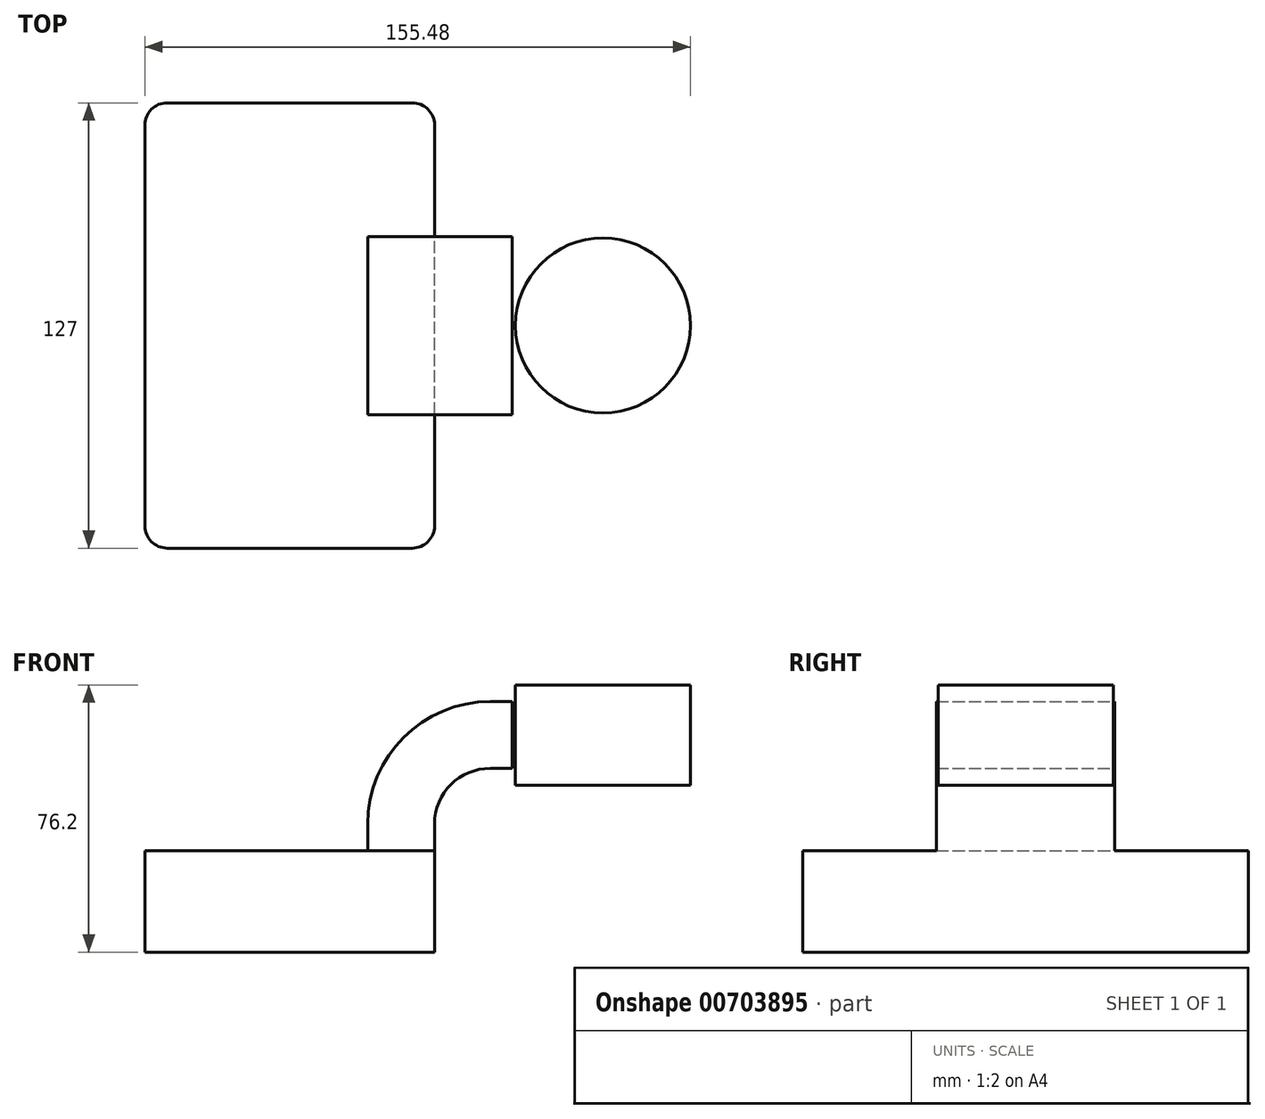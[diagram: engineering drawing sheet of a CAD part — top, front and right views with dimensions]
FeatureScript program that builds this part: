
annotation { "Feature Type Name" : "Feature", "Feature Type Description" : "" }
export const myFeature = defineFeature(function(context is Context, id is Id, definition is map)
    precondition{}
    {
        {
            var Q0;
            Q0=qCreatedBy(makeId("Front.planeOp"),FACE);
            var sketch = newSketch(context, id + "F0", { "sketchPlane" : qUnion([Q0])});
            skLineSegment(sketch, "E0.bottom", {"start": v(-41.27, 14.47) * mm, "end": v(41.27, 14.47) * mm});
            skLineSegment(sketch, "E0.top", {"start": v(-41.27, -14.47) * mm, "end": v(41.27, -14.47) * mm});
            skLineSegment(sketch, "E0.left", {"start": v(-41.28, 14.47) * mm, "end": v(-41.28, -14.47) * mm});
            skLineSegment(sketch, "E0.right", {"start": v(41.28, 14.47) * mm, "end": v(41.28, -14.47) * mm});
            skPoint(sketch, "E0.middle", {"position": v(0, 0) * mm});
            skLineSegment(sketch, "E1.bottom", {"start": v(114.21, 33.16) * mm, "end": v(63.41, 33.16) * mm});
            skLineSegment(sketch, "E1.top", {"start": v(114.21, 61.73) * mm, "end": v(63.41, 61.73) * mm});
            skLineSegment(sketch, "E1.left", {"start": v(114.21, 33.16) * mm, "end": v(114.21, 61.73) * mm});
            skLineSegment(sketch, "E1.right", {"start": v(63.41, 33.16) * mm, "end": v(63.41, 61.73) * mm});
            skPoint(sketch, "E1.middle", {"position": v(88.81, 47.44) * mm});
            skLineSegment(sketch, "E2", {"start": v(41.28, 14.47) * mm, "end": v(41.28, 22.06) * mm});
            skArc(sketch, "E3", {"start": v(41.28, 22.06) * mm, "mid": v(45.92, 33.28) * mm, "end": v(57.15, 37.93) * mm});
            skLineSegment(sketch, "E4", {"start": v(57.15, 37.93) * mm, "end": v(89.27, 37.93) * mm});
            skLineSegment(sketch, "E5", {"start": v(89.27, 37.93) * mm, "end": v(66.96, 37.93) * mm});
            skLineSegment(sketch, "E6.0", {"start": v(57.15, 56.98) * mm, "end": v(89.27, 56.98) * mm});
            skArc(sketch, "E6.1", {"start": v(22.23, 22.06) * mm, "mid": v(32.45, 46.75) * mm, "end": v(57.15, 56.98) * mm});
            skLineSegment(sketch, "E6.2", {"start": v(22.23, 14.47) * mm, "end": v(22.23, 22.06) * mm});
            skLineSegment(sketch, "E7", {"start": v(89.27, 33.16) * mm, "end": v(89.27, 61.73) * mm});
            skFitSpline(sketch, "E8", {"points": [v(-41.27, 14.47) * mm, v(57.15, 56.98) * mm], "startDerivative": vector(69.74, 94.52) * mm, "endDerivative": vector(102.79, -27.74) * mm});
            skSolve(sketch);
        }
        {
            var Q0;
            Q0=makeQuery(id+"F0.imprint","IMPRINT",FACE,{"disambiguationData":[TD([[makeQuery(id+"F0.imprint","IMPRINT",EDGE,{"derivedFrom":sQuery(id+"F0.wireOp",EDGE,"E0.top")}),1.0]])]});
            extrude(context, id + "F1", {"entities" : qUnion([Q0]), "endBound" : BoundingType.SYMMETRIC, "depth" : 127 * mm, "offsetDistance" : 25.4 * mm});
        }
        {
            var Q0;
            {var subQ1=sQuery(id+"F0.wireOp",EDGE,"E2");Q0=makeQuery(id+"F0.imprint","IMPRINT",FACE,{"disambiguationData":[TD([[makeQuery(id+"F0.imprint","IMPRINT",EDGE,{"derivedFrom":subQ1}),1.0]])]});}
            var sketch = newSketch(context, id + "F2", { "sketchPlane" : qUnion([Q0])});
            skSolve(sketch);
        }
        {
            var Q0;
            Q0 = qSketchRegion(id + "F2", true);
            var Q1;
            {var subQ1=sQuery(id+"F0.wireOp",EDGE,"E2");Q1=makeQuery(id+"F0.imprint","IMPRINT",FACE,{"disambiguationData":[TD([[makeQuery(id+"F0.imprint","IMPRINT",EDGE,{"derivedFrom":subQ1}),1.0]])]});}
            var Q2;
            {var subQ5=sQuery(id+"F0.wireOp",EDGE,"E5");Q2=makeQuery(id+"F0.imprint","IMPRINT",FACE,{"disambiguationData":[TD([[makeQuery(id+"F0.imprint","IMPRINT",EDGE,{"derivedFrom":subQ5}),-1.0]])]});}
            extrude(context, id + "F3", {"entities" : qUnion([Q0, Q1, Q2]), "operationType" : NewBodyOperationType.ADD, "endBound" : BoundingType.SYMMETRIC, "depth" : 50.8 * mm, "offsetDistance" : 25.4 * mm});
        }
        {
            var Q0;
            Q0=makeQuery(id+"F0.imprint","IMPRINT",FACE,{"disambiguationData":[TD([[makeQuery(id+"F0.imprint","IMPRINT",EDGE,{"derivedFrom":sQuery(id+"F0.wireOp",EDGE,"E6.1")}),1.0]])]});
            var sketch = newSketch(context, id + "F4", { "sketchPlane" : qUnion([Q0])});
            skSolve(sketch);
        }
        {
            var Q0;
            Q0 = qSketchRegion(id + "F4", true);
            var Q1;
            Q1=makeQuery(id+"F0.imprint","IMPRINT",FACE,{"disambiguationData":[TD([[makeQuery(id+"F0.imprint","IMPRINT",EDGE,{"derivedFrom":sQuery(id+"F0.wireOp",EDGE,"E6.1")}),1.0]])]});
            extrude(context, id + "F5", {"entities" : qUnion([Q0, Q1]), "operationType" : NewBodyOperationType.ADD, "endBound" : BoundingType.SYMMETRIC, "depth" : 15.88 * mm, "offsetDistance" : 25.4 * mm});
        }
        {
            var Q0;
            {var subQ0=sQuery(id+"F0.wireOp",EDGE,"E1.left");Q0=makeQuery(id+"F0.imprint","IMPRINT",FACE,{"disambiguationData":[TD([[makeQuery(id+"F0.imprint","IMPRINT",EDGE,{"derivedFrom":subQ0}),1.0]])]});}
            var Q1;
            Q1=sQuery(id+"F0.wireOp",EDGE,"E7");
            revolve(context, id + "F6", {"operationType" : NewBodyOperationType.ADD, "surfaceOperationType" : NewSurfaceOperationType.NEW, "entities" : qUnion([Q0]), "axis" : qUnion([Q1]), "revolveType" : RevolveType.FULL});
        }
        {
            var Q0;
            Q0=makeQuery(id+"F1.opExtrude","CAP_EDGE",EDGE,{"disambiguationData":[OSD([sQuery(id+"F0.wireOp",EDGE,"E0.left")])],"isStart":false});
            var Q1;
            Q1=makeQuery(id+"F1.opExtrude","CAP_EDGE",EDGE,{"disambiguationData":[OSD([sQuery(id+"F0.wireOp",EDGE,"E0.right")])],"isStart":false});
            var Q2;
            Q2=makeQuery(id+"F1.opExtrude","CAP_EDGE",EDGE,{"disambiguationData":[OSD([sQuery(id+"F0.wireOp",EDGE,"E0.right")])],"isStart":true});
            var Q3;
            Q3=makeQuery(id+"F1.opExtrude","CAP_EDGE",EDGE,{"disambiguationData":[OSD([sQuery(id+"F0.wireOp",EDGE,"E0.left")])],"isStart":true});
            fillet(context, id + "F7", {"entities" : qUnion([Q0, Q1, Q2, Q3]), "radius" : 6.35 * mm, "tangentPropagation" : true, "allowEdgeOverflow" : false});
        }
    });
